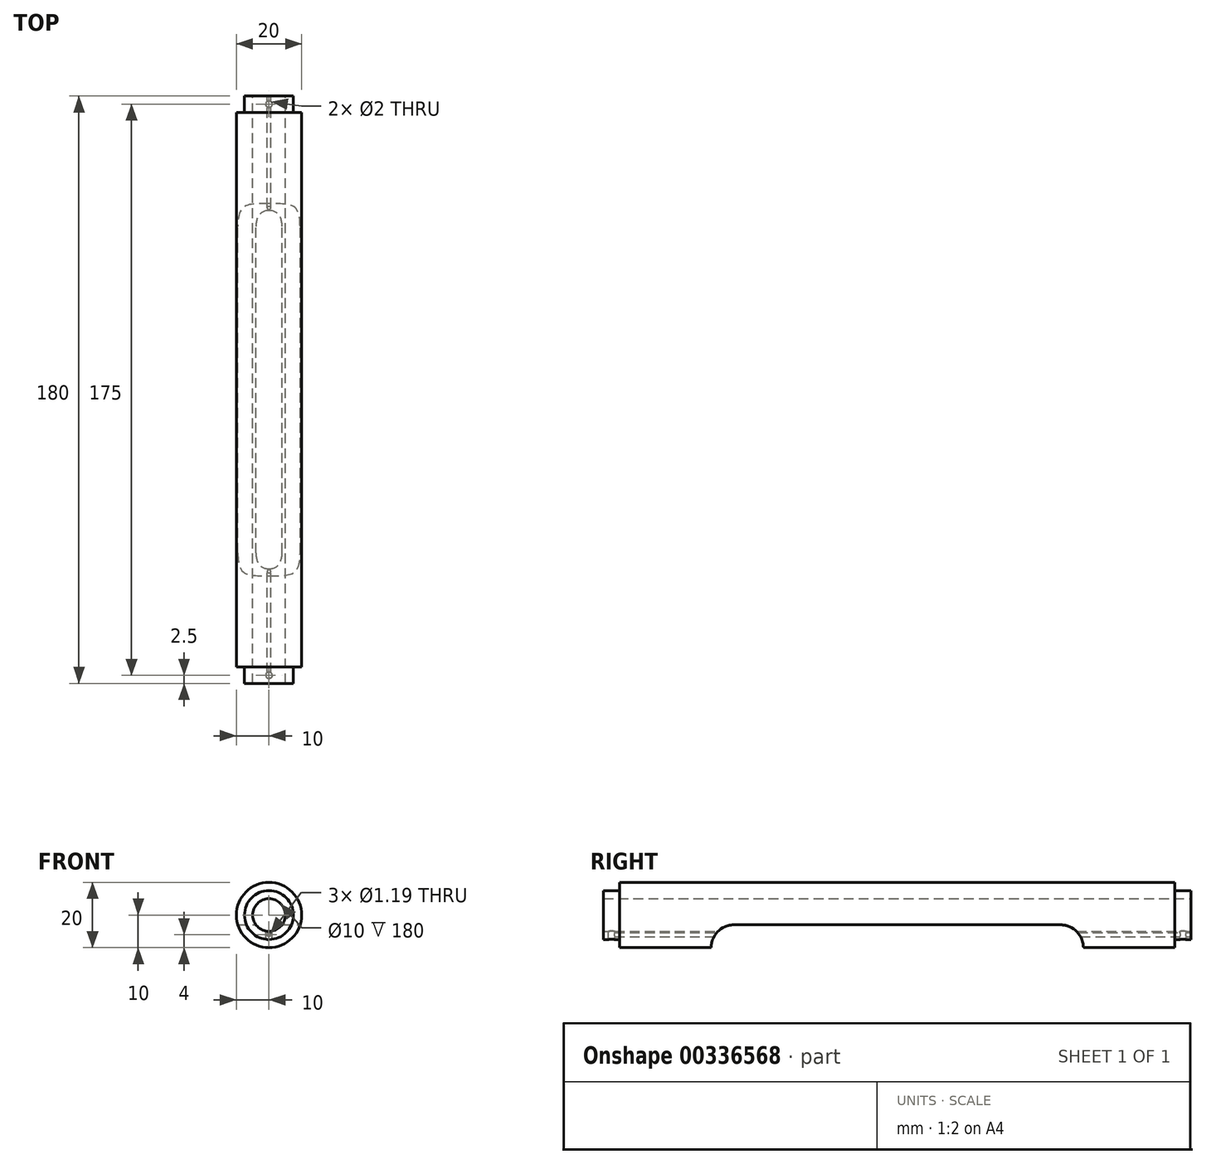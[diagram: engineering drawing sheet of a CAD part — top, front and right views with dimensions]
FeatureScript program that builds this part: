
annotation { "Feature Type Name" : "Feature", "Feature Type Description" : "" }
export const myFeature = defineFeature(function(context is Context, id is Id, definition is map)
    precondition{}
    {
        {
            var Q0;
            Q0=qCreatedBy(makeId("Front.planeOp"),FACE);
            var sketch = newSketch(context, id + "F0", { "sketchPlane" : qUnion([Q0])});
            skCircle(sketch, "E0", {"center": v(0, 0) * mm, "radius": 10 * mm});
            skCircle(sketch, "E1", {"center": v(0, 0) * mm, "radius": 5 * mm});
            skSolve(sketch);
        }
        {
            var Q0;
            Q0 = qSketchRegion(id + "F0", true);
            extrude(context, id + "F1", {"entities" : qUnion([Q0]), "depth" : 180 * mm});
        }
        {
            var Q0;
            Q0=qCreatedBy(makeId("Right.planeOp"),FACE);
            var sketch = newSketch(context, id + "F2", { "sketchPlane" : qUnion([Q0])});
            skLineSegment(sketch, "E2.bottom", {"start": v(-140, -3) * mm, "end": v(-40, -3) * mm});
            skLineSegment(sketch, "E2.top", {"start": v(-140, -17) * mm, "end": v(-40, -17) * mm});
            skArc(sketch, "E3", {"start": v(-140, -3) * mm, "mid": v(-147, -10) * mm, "end": v(-140, -17) * mm});
            skArc(sketch, "E4", {"start": v(-40, -17) * mm, "mid": v(-33, -10) * mm, "end": v(-40, -3) * mm});
            skSolve(sketch);
        }
        {
            var Q0;
            Q0 = qSketchRegion(id + "F2", true);
            extrude(context, id + "F3", {"entities" : qUnion([Q0]), "operationType" : NewBodyOperationType.REMOVE, "endBound" : BoundingType.SYMMETRIC, "oppositeDirection" : true, "depth" : 25 * mm});
        }
        {
            var Q0;
            Q0=makeQuery(id+"F1.opExtrude","CAP_FACE",FACE,{"disambiguationData":[OSD([sQuery(id+"F0.wireOp",EDGE,"E0"),sQuery(id+"F0.wireOp",EDGE,"E1")])],"isStart":true});
            var sketch = newSketch(context, id + "F4", { "sketchPlane" : qUnion([Q0])});
            skCircle(sketch, "E5", {"center": v(0, 0) * mm, "radius": 7.5 * mm});
            skSolve(sketch);
        }
        {
            var Q0;
            Q0=makeQuery(id+"F4.imprint","IMPRINT",FACE,{"disambiguationData":[TD([[makeQuery(id+"F4.imprint","IMPRINT",EDGE,{"derivedFrom":sQuery(id+"F4.wireOp",EDGE,"E5")}),-1.0]])]});
            extrude(context, id + "F5", {"entities" : qUnion([Q0]), "operationType" : NewBodyOperationType.REMOVE, "oppositeDirection" : true, "depth" : 5 * mm});
        }
        {
            var Q0;
            Q0=makeQuery(id+"F1.opExtrude","CAP_FACE",FACE,{"disambiguationData":[OSD([sQuery(id+"F0.wireOp",EDGE,"E0"),sQuery(id+"F0.wireOp",EDGE,"E1")])],"isStart":true});
            var sketch = newSketch(context, id + "F6", { "sketchPlane" : qUnion([Q0])});
            skCircle(sketch, "E6", {"center": v(0, -6) * mm, "radius": 0.6 * mm});
            skSolve(sketch);
        }
        {
            var Q0;
            Q0 = qSketchRegion(id + "F6", true);
            extrude(context, id + "F7", {"entities" : qUnion([Q0]), "operationType" : NewBodyOperationType.REMOVE, "oppositeDirection" : true, "depth" : 177 * mm});
        }
        {
            var Q0;
            Q0=qCreatedBy(makeId("Top.planeOp"),FACE);
            var sketch = newSketch(context, id + "F8", { "sketchPlane" : qUnion([Q0])});
            skCircle(sketch, "E7", {"center": v(0, -2.5) * mm, "radius": 1 * mm});
            skSolve(sketch);
        }
        {
            var Q0;
            Q0 = qSketchRegion(id + "F8", true);
            extrude(context, id + "F9", {"entities" : qUnion([Q0]), "operationType" : NewBodyOperationType.REMOVE, "oppositeDirection" : true, "depth" : 25 * mm});
        }
        {
            var Q0;
            Q0=makeQuery(id+"F1.opExtrude","CAP_FACE",FACE,{"disambiguationData":[OSD([sQuery(id+"F0.wireOp",EDGE,"E0"),sQuery(id+"F0.wireOp",EDGE,"E1")])],"isStart":false});
            var sketch = newSketch(context, id + "F10", { "sketchPlane" : qUnion([Q0])});
            skCircle(sketch, "E8", {"center": v(0, 0) * mm, "radius": 7.5 * mm});
            skSolve(sketch);
        }
        {
            var Q0;
            Q0=makeQuery(id+"F10.imprint","IMPRINT",FACE,{"disambiguationData":[TD([[makeQuery(id+"F10.imprint","IMPRINT",EDGE,{"derivedFrom":sQuery(id+"F10.wireOp",EDGE,"E8")}),-1.0]])]});
            extrude(context, id + "F11", {"entities" : qUnion([Q0]), "operationType" : NewBodyOperationType.REMOVE, "oppositeDirection" : true, "depth" : 5 * mm});
        }
        {
            var Q0;
            Q0=qCreatedBy(makeId("Top.planeOp"),FACE);
            var sketch = newSketch(context, id + "F12", { "sketchPlane" : qUnion([Q0])});
            skCircle(sketch, "E9", {"center": v(0, -177.5) * mm, "radius": 1 * mm});
            skSolve(sketch);
        }
        {
            var Q0;
            Q0 = qSketchRegion(id + "F12", true);
            extrude(context, id + "F13", {"entities" : qUnion([Q0]), "operationType" : NewBodyOperationType.REMOVE, "oppositeDirection" : true, "depth" : 25 * mm});
        }
    });
